# Revit family: Einbaugeräte_Modul_45-Systeme_Steckdose_0°_mit_Erdungsstift_1_fach
name_source: partatom
category: Generic Models
revit_build: Autodesk Revit 2015 (Build: 20140606_1530(x64)
units: mm (PartAtom-declared; Revit-internal decimal feet)

## types (6) — shared parameters
Manufacturer = OBO Bettermann
URL = http://www.obo-bettermann.com

## per-type parameters (varying)
| type | GTIN | Manufacturer Art. No. | Material |
| STD-F0 MZGN1 | 4012196048069 | 6120155 | Polycarbonate, minzgrün |
| STD-F0 ROR1 | 4012196048052 | 6120154 | Polycarbonate, reinorange |
| STD-F0 RW1 | 4012196048045 | 6120152 | Polycarbonate, Clear reinweiß |
| STD-F0 SRO1 | 4012196048113 | 6120158 | Polycarbonate, signalrot |
| STD-F0 AL1 | 4012196048175 | 6120162 | Polycarbonate,Alu lackiert |
| STD-F0 SWGR1 | 4012196048168 | 6120160 | Polycarbonate, schwarzgrau |

note: column(s) folded — value = type name in every type: Article Type

## geometry (parser evidence)
native form markers: Sweep x1
no freeform markers — native parametric forms only
